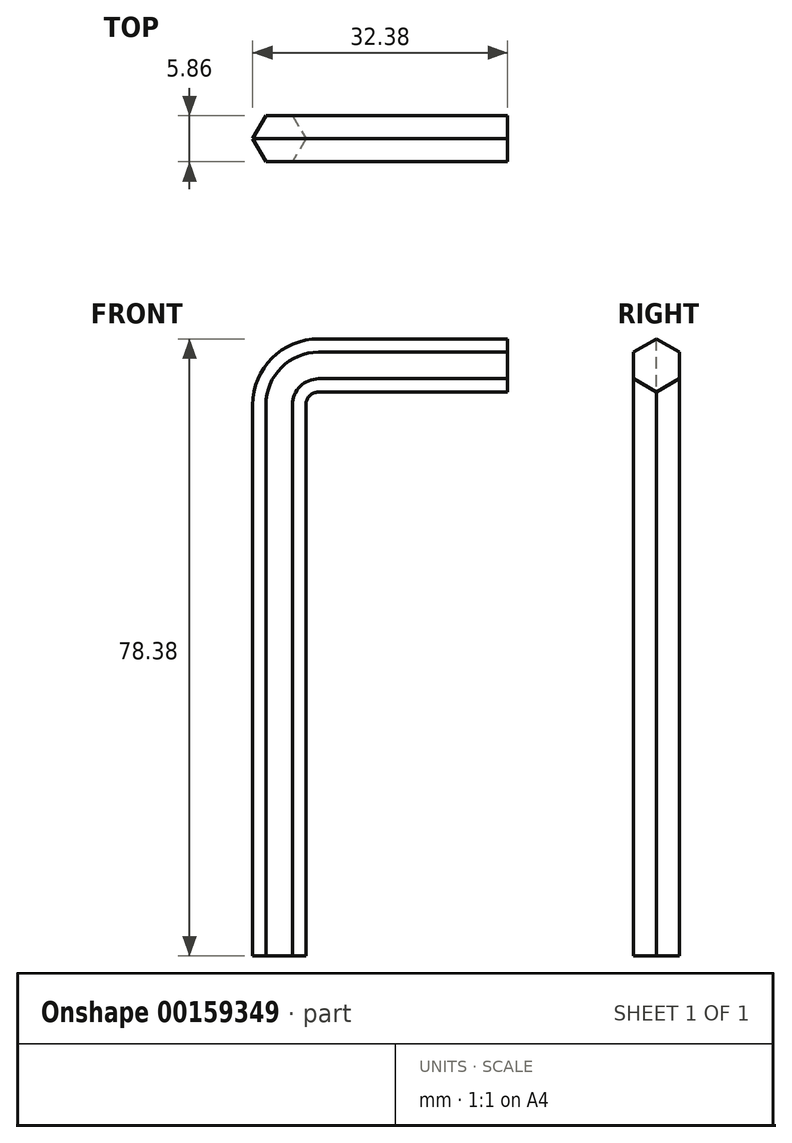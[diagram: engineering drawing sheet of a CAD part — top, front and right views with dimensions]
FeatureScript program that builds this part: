
annotation { "Feature Type Name" : "Feature", "Feature Type Description" : "" }
export const myFeature = defineFeature(function(context is Context, id is Id, definition is map)
    precondition{}
    {
        {
            var Q0;
            Q0=qCreatedBy(makeId("Top.planeOp"),FACE);
            var sketch = newSketch(context, id + "F0", { "sketchPlane" : qUnion([Q0])});
            skCircle(sketch, "E0.cCircle", {"center": v(0, 0) * mm, "radius": 2.93 * mm, "construction": true});
            skLineSegment(sketch, "E0.0", {"start": v(1.69, 2.93) * mm, "end": v(3.38, 0) * mm});
            skLineSegment(sketch, "E0.1", {"start": v(3.38, 0) * mm, "end": v(1.69, -2.93) * mm});
            skLineSegment(sketch, "E0.2", {"start": v(1.69, -2.93) * mm, "end": v(-1.69, -2.93) * mm});
            skLineSegment(sketch, "E0.3", {"start": v(-1.69, -2.93) * mm, "end": v(-3.38, 0) * mm});
            skLineSegment(sketch, "E0.4", {"start": v(-3.38, 0) * mm, "end": v(-1.69, 2.93) * mm});
            skLineSegment(sketch, "E0.5", {"start": v(-1.69, 2.93) * mm, "end": v(1.69, 2.93) * mm});
            skPoint(sketch, "E0.0.midPoint", {"position": v(2.53, 1.46) * mm});
            skSolve(sketch);
        }
        {
            var Q0;
            Q0=qCreatedBy(makeId("Front.planeOp"),FACE);
            var sketch = newSketch(context, id + "F1", { "sketchPlane" : qUnion([Q0])});
            skLineSegment(sketch, "E1", {"start": v(0, 0) * mm, "end": v(0, 70) * mm});
            skArc(sketch, "E2", {"start": v(5, 75) * mm, "mid": v(1.46, 73.54) * mm, "end": v(0, 70) * mm});
            skLineSegment(sketch, "E3", {"start": v(5, 75) * mm, "end": v(29, 75) * mm});
            skSolve(sketch);
        }
        {
            var Q0;
            Q0=makeQuery(id+"F0.imprint","IMPRINT",FACE,{"disambiguationData":[TD([[makeQuery(id+"F0.imprint","IMPRINT",EDGE,{"derivedFrom":sQuery(id+"F0.wireOp",EDGE,"E0.0")}),-1.0]])]});
            var Q1;
            Q1=sQuery(id+"F1.wireOp",EDGE,"E1");
            var Q2;
            Q2=sQuery(id+"F1.wireOp",EDGE,"E2");
            var Q3;
            Q3=sQuery(id+"F1.wireOp",EDGE,"E3");
            sweep(context, id + "F2", {"profiles" : qUnion([Q0]), "path" : qUnion([Q1, Q2, Q3])});
        }
    });
